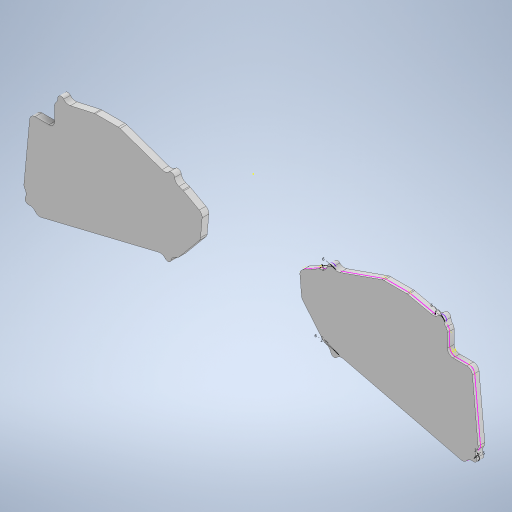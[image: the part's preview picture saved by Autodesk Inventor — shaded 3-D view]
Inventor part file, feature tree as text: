
AUTODESK INVENTOR PART (.ipt)
format: ipt  version: 2024 (Build 280153000, 153)  size: 488,448 bytes
history: native  units: mm
features: extrude x4, other x1, sketch x1, fillet x1, mirror x1
ambient origin geometry x8: Origin, YZ Plane, XZ Plane, XY Plane, X Axis, Y Axis, Z Axis, Center Point
bodies: Body1 (feature_tree)
feature tree (8):
  other  "Твердое тело1"
  sketch  "Эскиз2"
  extrude  "Выдавливание1"  Depth=2.0mm TaperAngle=0.0deg
  extrude  "Выдавливание2"  Depth=4.0mm TaperAngle=0.0deg
  extrude  "Выдавливание3"  Depth=6.0mm
  extrude  "Выдавливание4"  Depth=2.0mm
  fillet  "Сопряжение1"  Radius=6.0mm
  mirror  "Зеркальное отражение1"
